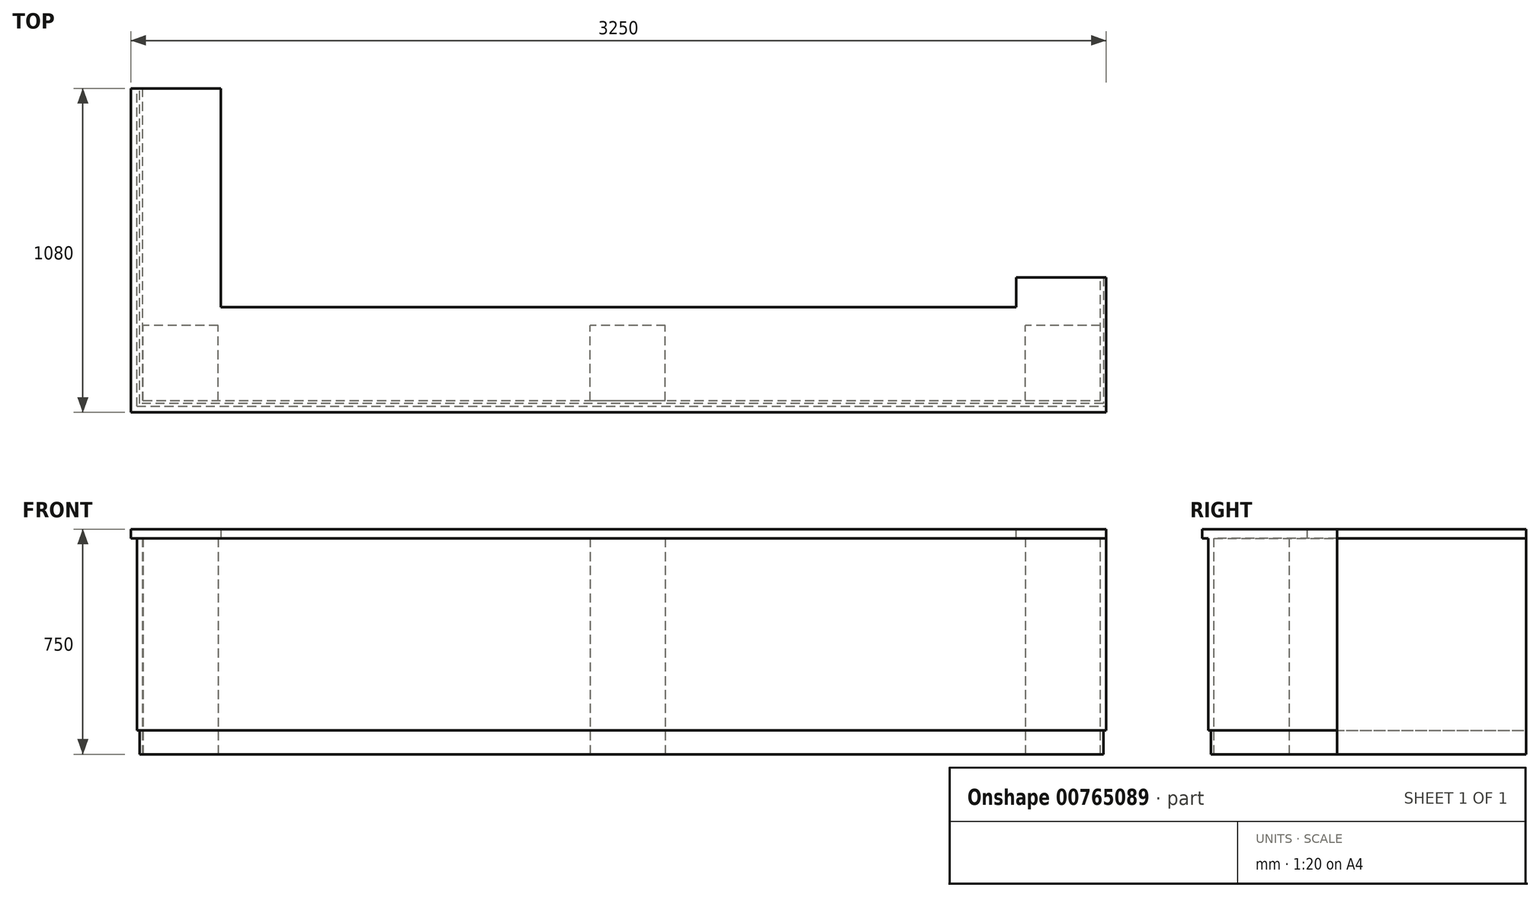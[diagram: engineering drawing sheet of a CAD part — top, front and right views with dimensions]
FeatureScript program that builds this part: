
annotation { "Feature Type Name" : "Feature", "Feature Type Description" : "" }
export const myFeature = defineFeature(function(context is Context, id is Id, definition is map)
    precondition{}
    {
        {
            var Q0;
            Q0=qCreatedBy(makeId("Top.planeOp"),FACE);
            cPlane(context, id + "F0", {"entities" : qUnion([Q0]), "cplaneType" : CPlaneType.OFFSET, "offset" : 770 * mm, "width" : 150 * mm, "height" : 150 * mm});
        }
        {
            var Q0;
            Q0=qCreatedBy(id+"F0.planeOp",FACE);
            var sketch = newSketch(context, id + "F1", { "sketchPlane" : qUnion([Q0])});
            skLineSegment(sketch, "E0", {"start": v(0, 0) * mm, "end": v(0, 1080) * mm});
            skLineSegment(sketch, "E1", {"start": v(0, 0) * mm, "end": v(3250, 0) * mm});
            skLineSegment(sketch, "E2", {"start": v(0, 1080) * mm, "end": v(300, 1080) * mm});
            skLineSegment(sketch, "E3", {"start": v(300, 1080) * mm, "end": v(300, 350) * mm});
            skLineSegment(sketch, "E4", {"start": v(300, 350) * mm, "end": v(3250, 350) * mm});
            skLineSegment(sketch, "E5", {"start": v(3250, 350) * mm, "end": v(3250, 0) * mm});
            skSolve(sketch);
        }
        {
            var Q0;
            Q0=makeQuery(id+"F1.imprint","IMPRINT",FACE,{"disambiguationData":[TD([[makeQuery(id+"F1.imprint","IMPRINT",EDGE,{"derivedFrom":sQuery(id+"F1.wireOp",EDGE,"E0")}),-1.0]])]});
            extrude(context, id + "F2", {"entities" : qUnion([Q0]), "depth" : 30 * mm, "offsetDistance" : 25 * mm});
        }
        {
            var Q0;
            Q0=makeQuery(id+"F2.opExtrude","CAP_FACE",FACE,{"disambiguationData":[OSD([sQuery(id+"F1.wireOp",EDGE,"E0"),sQuery(id+"F1.wireOp",EDGE,"E1"),sQuery(id+"F1.wireOp",EDGE,"E2"),sQuery(id+"F1.wireOp",EDGE,"E3"),sQuery(id+"F1.wireOp",EDGE,"E4"),sQuery(id+"F1.wireOp",EDGE,"E5")])],"isStart":true});
            var sketch = newSketch(context, id + "F3", { "sketchPlane" : qUnion([Q0])});
            skLineSegment(sketch, "E6.0", {"start": v(0, 0) * mm, "end": v(0, -1080) * mm, "construction": true});
            skLineSegment(sketch, "E6.1", {"start": v(0, 0) * mm, "end": v(3250, 0) * mm, "construction": true});
            skLineSegment(sketch, "E7.0", {"start": v(20, -20) * mm, "end": v(20, -1080) * mm});
            skLineSegment(sketch, "E8.0", {"start": v(20, -20) * mm, "end": v(3250, -20) * mm});
            skLineSegment(sketch, "E9.0", {"start": v(39, -39) * mm, "end": v(39, -1080) * mm});
            skLineSegment(sketch, "E10.0", {"start": v(39, -39) * mm, "end": v(3250, -39) * mm});
            skLineSegment(sketch, "E11", {"start": v(20, -1080) * mm, "end": v(39, -1080) * mm});
            skLineSegment(sketch, "E12", {"start": v(3250, -39) * mm, "end": v(3250, -20) * mm});
            skSolve(sketch);
        }
        {
            var Q0;
            Q0=makeQuery(id+"F3.imprint","IMPRINT",FACE,{"disambiguationData":[TD([[makeQuery(id+"F3.imprint","IMPRINT",EDGE,{"derivedFrom":sQuery(id+"F3.wireOp",EDGE,"E7.0")}),1.0]])]});
            extrude(context, id + "F4", {"entities" : qUnion([Q0]), "depth" : 720 * mm, "offsetDistance" : 25 * mm});
        }
        {
            var Q0;
            Q0=makeQuery(id+"F2.opExtrude","CAP_FACE",FACE,{"disambiguationData":[OSD([sQuery(id+"F1.wireOp",EDGE,"E0"),sQuery(id+"F1.wireOp",EDGE,"E1"),sQuery(id+"F1.wireOp",EDGE,"E2"),sQuery(id+"F1.wireOp",EDGE,"E3"),sQuery(id+"F1.wireOp",EDGE,"E4"),sQuery(id+"F1.wireOp",EDGE,"E5")])],"isStart":false});
            var sketch = newSketch(context, id + "F5", { "sketchPlane" : qUnion([Q0])});
            skLineSegment(sketch, "E13", {"start": v(3250, 350) * mm, "end": v(3250, 450) * mm});
            skLineSegment(sketch, "E14", {"start": v(3250, 450) * mm, "end": v(2950, 450) * mm});
            skLineSegment(sketch, "E15", {"start": v(2950, 450) * mm, "end": v(2950, 350) * mm});
            skLineSegment(sketch, "E16", {"start": v(2950, 350) * mm, "end": v(3250, 350) * mm});
            skSolve(sketch);
        }
        {
            var Q0;
            Q0 = qSketchRegion(id + "F5", true);
            extrude(context, id + "F6", {"entities" : qUnion([Q0]), "operationType" : NewBodyOperationType.ADD, "oppositeDirection" : true, "depth" : 30 * mm, "offsetDistance" : 25 * mm});
        }
        {
            var Q0;
            Q0=makeQuery(id+"F4.opExtrude","SWEPT_FACE",FACE,{"disambiguationData":[OSD([sQuery(id+"F3.wireOp",EDGE,"E12")])]});
            var sketch = newSketch(context, id + "F7", { "sketchPlane" : qUnion([Q0])});
            skLineSegment(sketch, "E17", {"start": v(39, 50) * mm, "end": v(450, 50) * mm});
            skLineSegment(sketch, "E18", {"start": v(450, 50) * mm, "end": v(450, 770) * mm});
            skLineSegment(sketch, "E19", {"start": v(450, 770) * mm, "end": v(39, 770) * mm});
            skLineSegment(sketch, "E20", {"start": v(39, 770) * mm, "end": v(39, 50) * mm});
            skSolve(sketch);
        }
        {
            var Q0;
            Q0 = qSketchRegion(id + "F7", true);
            extrude(context, id + "F8", {"entities" : qUnion([Q0]), "operationType" : NewBodyOperationType.ADD, "oppositeDirection" : true, "depth" : 19 * mm, "offsetDistance" : 25 * mm});
        }
        {
            var Q0;
            Q0=makeQuery(id+"F8.boolean.opBoolean","MERGE",FACE,{"derivedFrom":[makeQuery(id+"F4.opExtrude","CAP_FACE",FACE,{"disambiguationData":[OSD([sQuery(id+"F3.wireOp",EDGE,"E7.0"),sQuery(id+"F3.wireOp",EDGE,"E8.0"),sQuery(id+"F3.wireOp",EDGE,"E9.0"),sQuery(id+"F3.wireOp",EDGE,"E10.0"),sQuery(id+"F3.wireOp",EDGE,"E11"),sQuery(id+"F3.wireOp",EDGE,"E12")])],"isStart":false}),makeQuery(id+"F8.opExtrude","SWEPT_FACE",FACE,{"disambiguationData":[OSD([sQuery(id+"F7.wireOp",EDGE,"E17")])]})]});
            var sketch = newSketch(context, id + "F9", { "sketchPlane" : qUnion([Q0])});
            skLineSegment(sketch, "E21.bottom", {"start": v(3231, -39) * mm, "end": v(2981, -39) * mm});
            skLineSegment(sketch, "E21.top", {"start": v(3231, -289) * mm, "end": v(2981, -289) * mm});
            skLineSegment(sketch, "E21.left", {"start": v(3231, -39) * mm, "end": v(3231, -289) * mm});
            skLineSegment(sketch, "E21.right", {"start": v(2981, -39) * mm, "end": v(2981, -289) * mm});
            skSolve(sketch);
        }
        {
            var Q0;
            Q0 = qSketchRegion(id + "F9", true);
            extrude(context, id + "F10", {"entities" : qUnion([Q0]), "oppositeDirection" : true, "depth" : 720 * mm, "offsetDistance" : 25 * mm});
        }
        {
            var Q0;
            Q0=makeQuery(id+"F10.opExtrude","SWEPT_BODY",BODY,{"disambiguationData":[OSD([sQuery(id+"F9.wireOp",EDGE,"E21.bottom"),sQuery(id+"F9.wireOp",EDGE,"E21.top"),sQuery(id+"F9.wireOp",EDGE,"E21.left"),sQuery(id+"F9.wireOp",EDGE,"E21.right")])]});
            transform(context, id + "F11", {"entities" : qUnion([Q0]), "transformType" : TransformType.TRANSLATION_3D, "dx" : -2940 * mm, "dy" : 0 * mm, "dz" : 0 * mm, "makeCopy" : true});
        }
        {
            var Q0;
            Q0=makeQuery(id+"F10.opExtrude","SWEPT_BODY",BODY,{"disambiguationData":[OSD([sQuery(id+"F9.wireOp",EDGE,"E21.bottom"),sQuery(id+"F9.wireOp",EDGE,"E21.top"),sQuery(id+"F9.wireOp",EDGE,"E21.left"),sQuery(id+"F9.wireOp",EDGE,"E21.right")])]});
            transform(context, id + "F12", {"entities" : qUnion([Q0]), "transformType" : TransformType.TRANSLATION_3D, "dx" : -1450 * mm, "dy" : 0 * mm, "dz" : 0 * mm, "makeCopy" : true});
        }
        {
            var Q0;
            Q0=makeQuery(id+"F8.boolean.opBoolean","MERGE",FACE,{"derivedFrom":[makeQuery(id+"F4.opExtrude","CAP_FACE",FACE,{"disambiguationData":[OSD([sQuery(id+"F3.wireOp",EDGE,"E7.0"),sQuery(id+"F3.wireOp",EDGE,"E8.0"),sQuery(id+"F3.wireOp",EDGE,"E9.0"),sQuery(id+"F3.wireOp",EDGE,"E10.0"),sQuery(id+"F3.wireOp",EDGE,"E11"),sQuery(id+"F3.wireOp",EDGE,"E12")])],"isStart":false}),makeQuery(id+"F8.opExtrude","SWEPT_FACE",FACE,{"disambiguationData":[OSD([sQuery(id+"F7.wireOp",EDGE,"E17")])]})]});
            var sketch = newSketch(context, id + "F13", { "sketchPlane" : qUnion([Q0])});
            skLineSegment(sketch, "E22", {"start": v(29.5, -1080) * mm, "end": v(20, -1080) * mm});
            skLineSegment(sketch, "E23", {"start": v(20, -1080) * mm, "end": v(20, -20) * mm});
            skLineSegment(sketch, "E24", {"start": v(20, -20) * mm, "end": v(3250, -20) * mm});
            skLineSegment(sketch, "E25", {"start": v(3250, -20) * mm, "end": v(3250, -450) * mm});
            skLineSegment(sketch, "E26", {"start": v(3250, -450) * mm, "end": v(3240.5, -450) * mm});
            skLineSegment(sketch, "E27", {"start": v(3240.5, -450) * mm, "end": v(3240.5, -29.5) * mm});
            skLineSegment(sketch, "E28", {"start": v(3240.5, -29.5) * mm, "end": v(29.5, -29.5) * mm});
            skLineSegment(sketch, "E29", {"start": v(29.5, -29.5) * mm, "end": v(29.5, -1080) * mm});
            skSolve(sketch);
        }
        {
            var Q0;
            Q0 = qSketchRegion(id + "F13", true);
            extrude(context, id + "F14", {"entities" : qUnion([Q0]), "operationType" : NewBodyOperationType.REMOVE, "oppositeDirection" : true, "depth" : 80 * mm, "offsetDistance" : 25 * mm});
        }
    });
